# Revit family: Indoor_Pendant Lamp_Santa&Cole_Cirio
name_source: partatom
category: Luminarias
revit_build: Autodesk Revit 2018 (Build: 20190510_1515(x64)
units: mm (PartAtom-declared; Revit-internal decimal feet)

## family parameters
Anfitrión = Cara
Compartido = No
Corte con vacíos al cargar = No
Cota de conector redondo = Diámetro de uso
Origen de luz = No
Punto de cálculo de habitación = No
Tipo de pieza = Normal

## types (1)
- Cirio Simple
    Assembly Instructions - CE = https://www.santacole.com
    Assembly Instructions - UL = https://www.santacole.com
    Carga aparente = 0 W
    Code = HEFxx+HEL0x+CIP0x
    Elevación por defecto = 1219 mm
    Energy Label = https://www.santacole.com
    Fabricante = Santa & Cole
    Load = 0 W
    Manufacturer website = http://www.santacole.com
    Modelo = Cirio Simple
    Technical Information = https://www.santacole.com
    URL = https://www.santacole.com

## geometry (parser evidence)
native form markers: Blend x4, Sweep x9
no freeform markers — native parametric forms only
